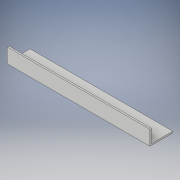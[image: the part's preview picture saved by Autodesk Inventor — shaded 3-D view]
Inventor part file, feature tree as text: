
AUTODESK INVENTOR PART (.ipt)
format: ipt  version: 2018 (Build 220112000, 112)  size: 103,424 bytes
history: native  units: in
note: dims shown in document units (in); Inventor stores cm internally (conversion verified against a paired STEP export)
features: extrude x2, sketch x2
ambient origin geometry x8: Origin, YZ Plane, XZ Plane, XY Plane, X Axis, Y Axis, Z Axis, Center Point
bodies: Solid1 (feature_tree)
feature tree (4):
  extrude  "Extrusion1"  Depth=1.755in
  extrude  "Extrusion2"  Depth=11.0in
  sketch  "Sketch1"  dims[d0=11.0in d1=1.755in]
  sketch  "Sketch2"  dims[d2=0.125in d3=0.0in d4=11.0in d5=0.125in d6=1.0in d7=0.0in]
